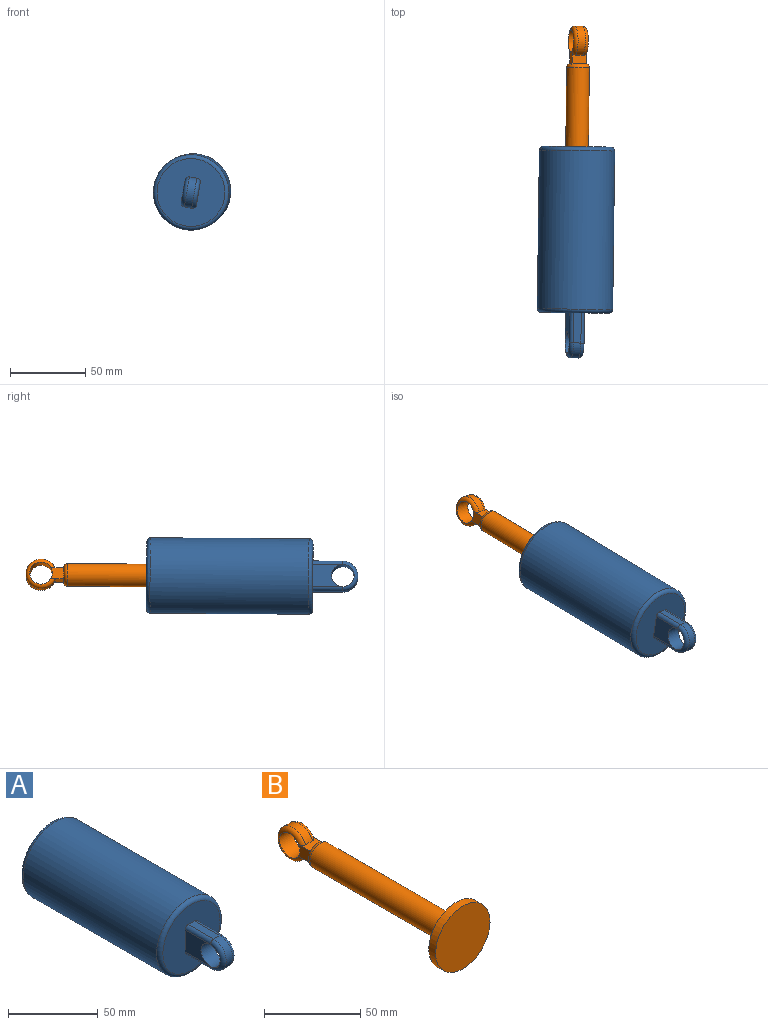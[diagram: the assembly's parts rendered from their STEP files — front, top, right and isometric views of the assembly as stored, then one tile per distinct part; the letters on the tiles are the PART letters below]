
ASSEMBLY  parts=2 mates=2
PART A: 21 faces, bbox 54.1x140.8x54.1 mm
  f0: plane 45x45mm, normal (0,-1,0), area 1395.8mm2, adj f7,f10,f11,f12,f13,f15,f16,f18
  f1: plane 40x40mm, normal (0,1,0), area 1256.6mm2, adj f2
  f2: cylinder r=20mm len=100mm, axis (0,1,0), area 12566.4mm2, adj f1,f3
  f3: plane 40x40mm, normal (0,-1,0), area 1079.9mm2, adj f2,f4
  f4: cylinder r=7.5mm len=15mm, axis (0,1,0), area 235.6mm2, adj f3,f5
  f5: plane 45x45mm, normal (0,1,0), area 1413.7mm2, adj f4,f20
  f6: cylinder r=25mm len=105mm, axis (0,1,0), area 16493.4mm2, adj f19,f20
  f7: plane 20x5mm, normal (0,0,1), area 100mm2, adj f0,f8,f13,f16
  f8: cylinder r=10mm len=20mm, axis (-1,0,0), area 157.1mm2, adj f7,f10,f14,f17
  f9: cylinder r=7.5mm len=15mm, axis (-1,0,0), area 471.2mm2, adj f11,f12,f14,f17
  f10: plane 20x5mm, normal (0,0,-1), area 100mm2, adj f0,f8,f15,f18
  f11: plane 20x15mm, normal (1,0,0), area 211.6mm2, adj f0,f9,f16,f18
  f12: plane 20x15mm, normal (-1,0,0), area 211.6mm2, adj f0,f9,f13,f15
  f13: cylinder r=2.5mm len=20mm, axis (0,-1,0), area 78.5mm2, adj f0,f7,f12,f14
  f14: torus R=7.5mm, axis (1,0,0), area 112.2mm2, adj f8,f9,f13,f15
  f15: cylinder r=2.5mm len=20mm, axis (0,1,0), area 78.5mm2, adj f0,f10,f12,f14
  f16: cylinder r=2.5mm len=20mm, axis (0,1,0), area 78.5mm2, adj f0,f7,f11,f17
  f17: torus R=7.5mm, axis (1,0,0), area 112.2mm2, adj f8,f9,f16,f18
  f18: cylinder r=2.5mm len=20mm, axis (0,-1,0), area 78.5mm2, adj f0,f10,f11,f17
  f19: torus R=22.5mm, axis (0,1,0), area 594.4mm2, adj f0,f6
  f20: torus R=22.5mm, axis (0,-1,0), area 594.4mm2, adj f5,f6
PART B: 15 faces, bbox 40.2x133.5x40.2 mm
  f0: plane 6.61x1.25mm, normal (0,1,0), area 5.7mm2, adj f6,f14
  f1: plane 40x40mm, normal (0,-1,0), area 1256.6mm2, adj f5
  f2: plane 6.61x1.25mm, normal (0,1,0), area 5.7mm2, adj f8,f14
  f3: cylinder r=7.5mm len=100mm, axis (0,1,0), area 4712.4mm2, adj f4,f14
  f4: plane 40x40mm, normal (0,1,0), area 1079.9mm2, adj f3,f5
  f5: cylinder r=20mm len=40mm, axis (0,1,0), area 628.3mm2, adj f1,f4
  f6: plane 10.17x9.01mm, normal (0,0,-1), area 60.6mm2, adj f0,f7,f10,f11,f12,f13,f14
  f7: cylinder r=10mm len=20mm, axis (-1,0,0), area 275.7mm2, adj f6,f8,f12,f13
  f8: plane 10.17x9.01mm, normal (0,0,1), area 60.6mm2, adj f2,f7,f10,f11,f12,f13,f14
  f9: cylinder r=7.5mm len=15mm, axis (-1,0,0), area 471.2mm2, adj f10,f11,f12,f13
  f10: plane 8.84x7.5mm, normal (1,0,0), area 59.2mm2, adj f6,f8,f9,f14
  f11: plane 8.84x7.5mm, normal (-1,0,0), area 59.2mm2, adj f6,f8,f9,f14
  f12: torus R=7.5mm, axis (1,0,0), area 193.9mm2, adj f6,f7,f8,f9
  f13: torus R=7.5mm, axis (1,0,0), area 193.9mm2, adj f6,f7,f8,f9
  f14: torus R=5mm, axis (0,-1,0), area 154.3mm2, adj f0,f2,f3,f6,f8,f10,f11
PLACE A rot(axis=(0.04,1,-0.07),9.8deg) t=(13.69,15.78,25.08)mm
PLACE B rot(axis=(0.03,1,-0.05),12.9deg) t=(14.41,73.28,25.45)mm
MATE cylindrical B.f3 <-> A.f2  axis (-0.01,-1,-0.01) through (14.41,73.28,25.45)mm
MATE parallel B.f3 <-> A.f2  axis (-0.01,-1,-0.01) through (14.41,73.28,25.45)mm
